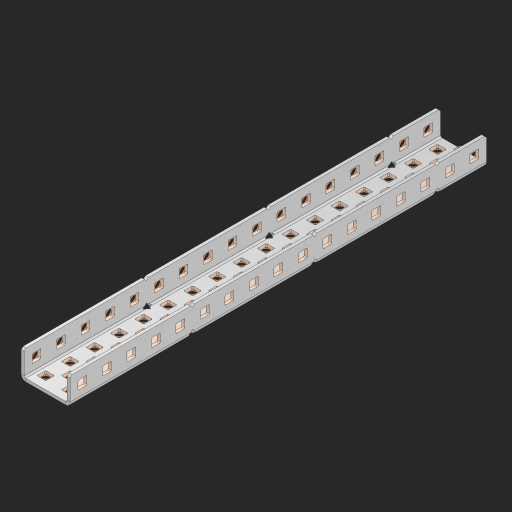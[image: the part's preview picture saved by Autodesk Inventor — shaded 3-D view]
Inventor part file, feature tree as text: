
AUTODESK INVENTOR PART (.ipt)
format: ipt  version: 2023 (Build 270158000, 158)  size: 1,257,984 bytes
history: native  units: in
note: dims shown in document units (in); Inventor stores cm internally (conversion verified against a paired STEP export)
features: other x92, extrude x83, sheet_metal_op x11, sketch x10, pattern_linear x2, mirror x1, chamfer x1
ambient origin geometry x8: Origin, YZ Plane, XZ Plane, XY Plane, X Axis, Y Axis, Z Axis, Center Point
bodies: Solid1 (feature_tree), Body (feature_tree)
feature tree (200):
  sheet_metal_op  "Flanges"
  other  "Flange Pattern Plane"
  other  "Flange Pattern Sketch"
  sheet_metal_op  "Flange Pattern"
  sheet_metal_op  "Body Pattern"
  pattern_linear  "Center Pattern"  Spacing1=0.0625in  [1 undecoded]
  other  "Arc Length"
  mirror  "Notch Mirror"
  pattern_linear  "Notch Pattern"  Spacing1=0.182in  [1 undecoded]
  chamfer  "End Chamfer"
  extrude  "Half Cut"  Depth=0.02in
  sketch  "Sketch1"  dims[d0=1.0in]
  other  "Plate1"
  sketch  "Sketch2"  dims[d1=8.5in]
  other  "Plate2"
  sheet_metal_op  "Bend1"
  sheet_metal_op  "Corner1"
  sketch  "Sketch3"  dims[d2=0.0625in]
  sketch  "Sketch7"  dims[d3=0.0625in]
  other  "Srf1"
  other  "Srf2"
  sketch  "Sketch8"  dims[d4=0.0312in]
  sketch  "Sketch9"  dims[d5=0.125in]
  other  "Srf91"
  sheet_metal_op  "Body Pattern Sketch"
  other  "Srf92"
  sketch  "Sketch13"  dims[d6=0.0625in]
  sketch  "Sketch14"  dims[d7=0.5in d8=90.0deg d9=0.0312in]
  sketch  "Sketch15"  dims[d10=0.25in]
  sketch  "Sketch16"  dims[d11=0.0625in d12=0.0625in d16=0.182in d17=0.02in d18=0.0625in d19=0.0in d20=0.25in d21=0.25in d38=6.6929in d40=0.5in d41=0.7874in d43=1.0in d46=0.172in d47=1.0in d48=0.0in d49=0.182in d50=0.02in d51=0.25in d52=0.25in d53=0.0625in d54=0.0in d55=0.172in d56=1.0in d57=0.0in d58=0.25in d60=6.6929in d62=0.5in d63=0.7874in d65=0.5in d85=0.1473in d86=0.1782in d88=0.04in d89=0.0625in d90=0.0in d91=0.04in d92=0.0491in d95=2.5in d96=0.04in d97=0.25in d98=45.0deg d99=0.25in d100=0.5in d101=0.0in d102=2.497in d106=0.182in d107=0.02in d108=0.5in d109=0.5in d110=0.0625in d111=0.0in d112=0.172in d113=0.5in d114=0.0in d117=0.5in d118=0.5in d119=0.5in]
  other  "Srf786"
  other  "Srf823"
  other  "Srf824"
  other  "Srf825"
  other  "Srf826"
  other  "Srf827"
  other  "Srf828"
  other  "Srf829"
  other  "Srf856"
  other  "Srf857"
  other  "Srf858"
  other  "Srf859"
  other  "Srf860"
  other  "Srf861"
  other  "Srf862"
  other  "Srf889"
  other  "Srf890"
  other  "Srf891"
  other  "Srf892"
  other  "Srf893"
  other  "Srf894"
  other  "Srf895"
  other  "Srf896"
  other  "Srf922"
  other  "Srf923"
  other  "Srf924"
  other  "Srf925"
  other  "Srf926"
  other  "Srf959"
  other  "Srf960"
  other  "Srf961"
  other  "Srf962"
  other  "Srf963"
  other  "Srf996"
  other  "Srf997"
  other  "Srf998"
  other  "Srf999"
  other  "Srf1000"
  other  "Srf1143"
  other  "Srf1144"
  other  "Srf1145"
  other  "Srf1146"
  other  "Srf1147"
  other  "Srf1148"
  other  "Srf1149"
  other  "Srf1150"
  other  "Srf1151"
  other  "Srf1152"
  other  "Srf1153"
  other  "Srf1154"
  other  "Srf1155"
  other  "Srf1156"
  other  "Srf1157"
  other  "Srf1158"
  other  "Srf1159"
  other  "Srf1160"
  other  "Srf1161"
  other  "Srf1162"
  other  "Srf1199"
  other  "Srf1200"
  other  "Srf1201"
  other  "Srf1202"
  other  "Srf1203"
  other  "Srf1204"
  other  "Srf1205"
  other  "Srf1206"
  other  "Srf1207"
  other  "Srf1208"
  other  "Srf1209"
  other  "Srf1210"
  other  "Srf1211"
  other  "Srf1212"
  other  "Srf1213"
  other  "Srf1214"
  other  "Srf1215"
  other  "Srf1216"
  other  "Srf1217"
  other  "Srf1218"
  other  "Srf1255"
  other  "Srf1256"
  other  "Srf1257"
  sheet_metal_op  "Flange Stamp"
  sheet_metal_op  "Flange Circle"
  sheet_metal_op  "Body Stamp"
  sheet_metal_op  "Body Circle"
  other  "Center Stamp"
  other  "Center Circle"
  sheet_metal_op  "Notch"
  extrude  "ExtrusionSrf2"  Depth=0.0625in
  extrude  "ExtrusionSrf92"  TaperAngle=0.0deg  [1 undecoded]
  extrude  "ExtrusionSrf823"  Depth=0.5in
  extrude  "ExtrusionSrf824"  Depth=0.5in
  extrude  "ExtrusionSrf825"  Depth=0.5in
  extrude  "ExtrusionSrf826"  Depth=0.5in
  extrude  "ExtrusionSrf827"  Depth=1.0in TaperAngle=0.0deg
  extrude  "ExtrusionSrf828"  Depth=0.5in
  extrude  "ExtrusionSrf829"  Depth=0.02in
  extrude  "ExtrusionSrf856"  Depth=0.5in
  extrude  "ExtrusionSrf857"  Depth=0.5in
  extrude  "ExtrusionSrf858"  Depth=0.0625in
  extrude  "ExtrusionSrf859"  TaperAngle=0.0deg  [1 undecoded]
  extrude  "ExtrusionSrf860"  Depth=0.5in
  extrude  "ExtrusionSrf861"  Depth=1.0in TaperAngle=0.0deg
  extrude  "ExtrusionSrf862"  Depth=0.5in
  extrude  "ExtrusionSrf889"  Depth=0.5in
  extrude  "ExtrusionSrf890"  Depth=0.5in
  extrude  "ExtrusionSrf891"  Depth=0.5in
  extrude  "ExtrusionSrf892"  Depth=0.5in
  extrude  "ExtrusionSrf893"  Depth=0.5in
  extrude  "ExtrusionSrf894"  Depth=0.0625in
  extrude  "ExtrusionSrf895"  TaperAngle=0.0deg  [1 undecoded]
  extrude  "ExtrusionSrf896"  Depth=0.5in
  extrude  "ExtrusionSrf922"  Depth=0.5in
  extrude  "ExtrusionSrf923"  Depth=2.5in
  extrude  "ExtrusionSrf924"  Depth=0.5in TaperAngle=45.0deg
  extrude  "ExtrusionSrf925"  Depth=0.5in
  extrude  "ExtrusionSrf926"  Depth=0.5in TaperAngle=0.0deg
  extrude  "ExtrusionSrf959"  Depth=0.5in
  extrude  "ExtrusionSrf960"  Depth=0.5in
  extrude  "ExtrusionSrf961"  Depth=0.02in
  extrude  "ExtrusionSrf962"  Depth=0.5in
  extrude  "ExtrusionSrf963"  Depth=0.5in
  extrude  "ExtrusionSrf996"  Depth=0.0625in
  extrude  "ExtrusionSrf997"  TaperAngle=0.0deg  [1 undecoded]
  extrude  "ExtrusionSrf998"  Depth=0.5in
  extrude  "ExtrusionSrf999"  Depth=0.5in TaperAngle=0.0deg
  extrude  "ExtrusionSrf1000"  Depth=0.5in
  extrude  "ExtrusionSrf1143"  Depth=0.5in
  extrude  "ExtrusionSrf1144"  Depth=0.5in
  extrude  "ExtrusionSrf1145"  [1 undecoded]
  extrude  "ExtrusionSrf1146"  [1 undecoded]
  extrude  "ExtrusionSrf1147"  [1 undecoded]
  extrude  "ExtrusionSrf1148"  [1 undecoded]
  extrude  "ExtrusionSrf1149"  [1 undecoded]
  extrude  "ExtrusionSrf1150"  [1 undecoded]
  extrude  "ExtrusionSrf1151"  [1 undecoded]
  extrude  "ExtrusionSrf1152"  [1 undecoded]
  extrude  "ExtrusionSrf1153"  [1 undecoded]
  extrude  "ExtrusionSrf1154"  [1 undecoded]
  extrude  "ExtrusionSrf1155"  [1 undecoded]
  extrude  "ExtrusionSrf1156"  [1 undecoded]
  extrude  "ExtrusionSrf1157"  [1 undecoded]
  extrude  "ExtrusionSrf1158"  [1 undecoded]
  extrude  "ExtrusionSrf1159"  [1 undecoded]
  extrude  "ExtrusionSrf1160"  [1 undecoded]
  extrude  "ExtrusionSrf1161"  [1 undecoded]
  extrude  "ExtrusionSrf1162"  [1 undecoded]
  extrude  "ExtrusionSrf1199"  [1 undecoded]
  extrude  "ExtrusionSrf1200"  [1 undecoded]
  extrude  "ExtrusionSrf1201"  [1 undecoded]
  extrude  "ExtrusionSrf1202"  [1 undecoded]
  extrude  "ExtrusionSrf1203"  [1 undecoded]
  extrude  "ExtrusionSrf1204"  [1 undecoded]
  extrude  "ExtrusionSrf1205"  [1 undecoded]
  extrude  "ExtrusionSrf1206"  [1 undecoded]
  extrude  "ExtrusionSrf1207"  [1 undecoded]
  extrude  "ExtrusionSrf1208"  [1 undecoded]
  extrude  "ExtrusionSrf1209"  [1 undecoded]
  extrude  "ExtrusionSrf1210"  [1 undecoded]
  extrude  "ExtrusionSrf1211"  [1 undecoded]
  extrude  "ExtrusionSrf1212"  [1 undecoded]
  extrude  "ExtrusionSrf1213"  [1 undecoded]
  extrude  "ExtrusionSrf1214"  [1 undecoded]
  extrude  "ExtrusionSrf1215"  [1 undecoded]
  extrude  "ExtrusionSrf1216"  [1 undecoded]
  extrude  "ExtrusionSrf1217"  [1 undecoded]
  extrude  "ExtrusionSrf1218"  [1 undecoded]
  extrude  "ExtrusionSrf1255"  [1 undecoded]
  extrude  "ExtrusionSrf1256"  [1 undecoded]
  extrude  "ExtrusionSrf1257"  [1 undecoded]
note: 47 required parameter values undecoded (feature->parameter linkage not recoverable at this tier; creation-order binding heuristic only, values carry confidence <= 0.55)
